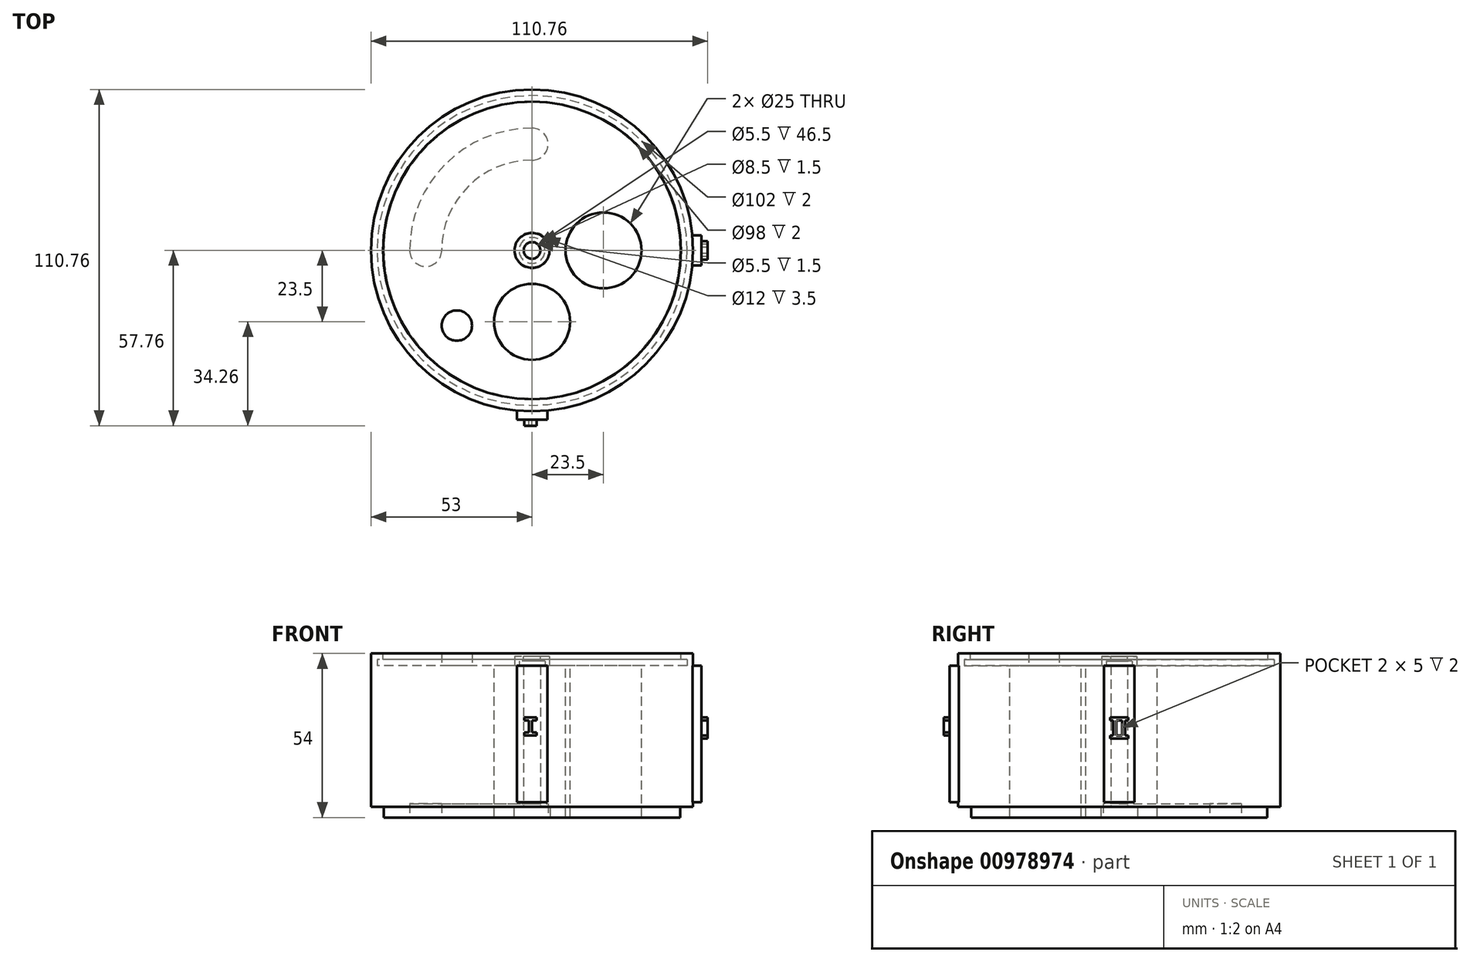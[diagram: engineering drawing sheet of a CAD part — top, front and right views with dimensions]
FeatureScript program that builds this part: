
annotation { "Feature Type Name" : "Feature", "Feature Type Description" : "" }
export const myFeature = defineFeature(function(context is Context, id is Id, definition is map)
    precondition{}
    {
        {
            var Q0;
            Q0=qCreatedBy(makeId("Top.planeOp"),FACE);
            var sketch = newSketch(context, id + "F0", { "sketchPlane" : qUnion([Q0])});
            skCircle(sketch, "E0", {"center": v(0, 0) * mm, "radius": 53 * mm});
            skCircle(sketch, "E1", {"center": v(0, 0) * mm, "radius": 2.75 * mm});
            skSolve(sketch);
        }
        {
            var Q0;
            Q0=makeQuery(id+"F0.imprint","IMPRINT",FACE,{"disambiguationData":[TD([[makeQuery(id+"F0.imprint","IMPRINT",EDGE,{"derivedFrom":sQuery(id+"F0.wireOp",EDGE,"E0")}),1.0]])]});
            extrude(context, id + "F1", {"entities" : qUnion([Q0]), "depth" : 50 * mm, "offsetDistance" : 25 * mm});
        }
        {
            var Q0;
            Q0=makeQuery(id+"F1.opExtrude","CAP_FACE",FACE,{"disambiguationData":[OSD([sQuery(id+"F0.wireOp",EDGE,"E0"),sQuery(id+"F0.wireOp",EDGE,"E1")])],"isStart":false});
            var sketch = newSketch(context, id + "F2", { "sketchPlane" : qUnion([Q0])});
            skCircle(sketch, "E2", {"center": v(0, 0) * mm, "radius": 51 * mm});
            skCircle(sketch, "E3", {"center": v(0, 0) * mm, "radius": 4.25 * mm});
            skCircle(sketch, "E4", {"center": v(0, 0) * mm, "radius": 5.75 * mm});
            skCircle(sketch, "E5", {"center": v(0, -23.5) * mm, "radius": 12.5 * mm});
            skCircle(sketch, "E6", {"center": v(23.5, 0) * mm, "radius": 12.5 * mm});
            skLineSegment(sketch, "E7", {"start": v(-5, -52.76) * mm, "end": v(-5, -55.76) * mm});
            skLineSegment(sketch, "E8", {"start": v(-5, -55.76) * mm, "end": v(5, -55.76) * mm});
            skLineSegment(sketch, "E9", {"start": v(5, -55.76) * mm, "end": v(5, -52.76) * mm});
            skLineSegment(sketch, "E10", {"start": v(52.76, 5) * mm, "end": v(55.76, 5) * mm});
            skLineSegment(sketch, "E11", {"start": v(55.76, 5) * mm, "end": v(55.76, -5) * mm});
            skLineSegment(sketch, "E12", {"start": v(55.76, -5) * mm, "end": v(52.76, -5) * mm});
            skLineSegment(sketch, "E13", {"start": v(0, 0) * mm, "end": v(-24.75, -24.75) * mm});
            skCircle(sketch, "E14", {"center": v(-24.75, -24.75) * mm, "radius": 5 * mm});
            skSolve(sketch);
        }
        {
            var Q0;
            Q0=makeQuery(id+"F2.imprint","IMPRINT",FACE,{"disambiguationData":[TD([[makeQuery(id+"F2.imprint","IMPRINT",EDGE,{"derivedFrom":sQuery(id+"F2.wireOp",EDGE,"E2")}),-1.0]])]});
            extrude(context, id + "F3", {"entities" : qUnion([Q0]), "operationType" : NewBodyOperationType.ADD, "depth" : 4 * mm, "offsetDistance" : 25 * mm});
        }
        {
            var Q0;
            Q0=makeQuery(id+"F3.opExtrude","CAP_FACE",FACE,{"disambiguationData":[OSD([sQuery(id+"F0.wireOp",EDGE,"E0"),sQuery(id+"F2.wireOp",EDGE,"E2")])],"isStart":false});
            var sketch = newSketch(context, id + "F4", { "sketchPlane" : qUnion([Q0])});
            skCircle(sketch, "E15", {"center": v(0, 0) * mm, "radius": 49 * mm});
            skSolve(sketch);
        }
        {
            var Q0;
            Q0=makeQuery(id+"F4.imprint","IMPRINT",FACE,{"disambiguationData":[TD([[makeQuery(id+"F4.imprint","IMPRINT",EDGE,{"derivedFrom":sQuery(id+"F4.wireOp",EDGE,"E15")}),-1.0]])]});
            extrude(context, id + "F5", {"entities" : qUnion([Q0]), "operationType" : NewBodyOperationType.ADD, "oppositeDirection" : true, "depth" : 2 * mm, "offsetDistance" : 25 * mm});
        }
        {
            var Q0;
            Q0=makeQuery(id+"F2.imprint","IMPRINT",FACE,{"disambiguationData":[TD([[makeQuery(id+"F2.imprint","IMPRINT",EDGE,{"derivedFrom":sQuery(id+"F2.wireOp",EDGE,"E3")}),-1.0]])]});
            extrude(context, id + "F6", {"entities" : qUnion([Q0]), "operationType" : NewBodyOperationType.ADD, "depth" : 3 * mm, "offsetDistance" : 25 * mm});
        }
        {
            var Q0;
            Q0=makeQuery(id+"F6.opExtrude","CAP_FACE",FACE,{"disambiguationData":[OSD([sQuery(id+"F2.wireOp",EDGE,"E3"),sQuery(id+"F2.wireOp",EDGE,"E4")])],"isStart":false});
            var sketch = newSketch(context, id + "F7", { "sketchPlane" : qUnion([Q0])});
            skCircle(sketch, "E16", {"center": v(0, 0) * mm, "radius": 2.75 * mm});
            skSolve(sketch);
        }
        {
            var Q0;
            Q0=makeQuery(id+"F7.imprint","IMPRINT",FACE,{"disambiguationData":[TD([[makeQuery(id+"F7.imprint","IMPRINT",EDGE,{"derivedFrom":sQuery(id+"F7.wireOp",EDGE,"E16")}),-1.0]])]});
            extrude(context, id + "F8", {"entities" : qUnion([Q0]), "operationType" : NewBodyOperationType.ADD, "oppositeDirection" : true, "depth" : 1.5 * mm, "offsetDistance" : 25 * mm});
        }
        {
            var Q0;
            Q0=makeQuery(id+"F1.opExtrude","CAP_FACE",FACE,{"disambiguationData":[OSD([sQuery(id+"F0.wireOp",EDGE,"E0"),sQuery(id+"F0.wireOp",EDGE,"E1")])],"isStart":true});
            var sketch = newSketch(context, id + "F9", { "sketchPlane" : qUnion([Q0])});
            skCircle(sketch, "E17", {"center": v(0, 0) * mm, "radius": 48.75 * mm});
            skCircle(sketch, "E18", {"center": v(0, 0) * mm, "radius": 6 * mm});
            skCircle(sketch, "E19", {"center": v(0, -35) * mm, "radius": 5.25 * mm});
            skCircle(sketch, "E20", {"center": v(-35, 0) * mm, "radius": 5.25 * mm});
            skCircle(sketch, "E21", {"center": v(0, 0) * mm, "radius": 29.75 * mm});
            skCircle(sketch, "E22", {"center": v(0, 0) * mm, "radius": 40.25 * mm});
            skSolve(sketch);
        }
        {
            var Q0;
            Q0=makeQuery(id+"F9.imprint","IMPRINT",FACE,{"disambiguationData":[TD([[makeQuery(id+"F9.imprint","IMPRINT",EDGE,{"derivedFrom":sQuery(id+"F9.wireOp",EDGE,"E17")}),-1.0]])]});
            var Q1;
            Q1=makeQuery(id+"F9.imprint","IMPRINT",FACE,{"disambiguationData":[TD([[makeQuery(id+"F9.imprint","IMPRINT",EDGE,{"derivedFrom":sQuery(id+"F9.wireOp",EDGE,"E18")}),1.0]])]});
            extrude(context, id + "F10", {"entities" : qUnion([Q0, Q1]), "operationType" : NewBodyOperationType.REMOVE, "oppositeDirection" : true, "depth" : 3.5 * mm, "offsetDistance" : 25 * mm});
        }
        {
            var Q0;
            {var subQ0=sQuery(id+"F9.wireOp",EDGE,"E20");var subQ1=makeQuery(id+"F9.imprint","INTERSECT",VERTEX,{"derivedFrom":[subQ0,sQuery(id+"F9.wireOp",EDGE,"E21")]});Q0=makeQuery(id+"F9.imprint","IMPRINT",FACE,{"disambiguationData":[TD([[makeQuery(id+"F9.imprint","IMPRINT",EDGE,{"disambiguationData":[TD([[subQ1,-1.0]])],"derivedFrom":subQ0}),1.0]])]});}
            var Q1;
            {var subQ0=sQuery(id+"F9.wireOp",EDGE,"E21");var subQ1=sQuery(id+"F9.wireOp",EDGE,"E19");var subQ2=makeQuery(id+"F9.imprint","INTERSECT",VERTEX,{"derivedFrom":[subQ1,subQ0]});Q1=makeQuery(id+"F9.imprint","IMPRINT",FACE,{"disambiguationData":[TD([[makeQuery(id+"F9.imprint","IMPRINT",EDGE,{"disambiguationData":[TD([[subQ2,-1.0]])],"derivedFrom":subQ1}),-1.0]])]});}
            var Q2;
            {var subQ0=sQuery(id+"F9.wireOp",EDGE,"E19");var subQ1=makeQuery(id+"F9.imprint","INTERSECT",VERTEX,{"derivedFrom":[subQ0,sQuery(id+"F9.wireOp",EDGE,"E21")]});Q2=makeQuery(id+"F9.imprint","IMPRINT",FACE,{"disambiguationData":[TD([[makeQuery(id+"F9.imprint","IMPRINT",EDGE,{"disambiguationData":[TD([[subQ1,-1.0]])],"derivedFrom":subQ0}),1.0]])]});}
            extrude(context, id + "F11", {"entities" : qUnion([Q0, Q1, Q2]), "operationType" : NewBodyOperationType.REMOVE, "oppositeDirection" : true, "depth" : 4.5 * mm, "offsetDistance" : 25 * mm});
        }
        {
            var Q0;
            Q0=makeQuery(id+"F2.imprint","IMPRINT",FACE,{"disambiguationData":[TD([[makeQuery(id+"F2.imprint","IMPRINT",EDGE,{"derivedFrom":sQuery(id+"F2.wireOp",EDGE,"E6")}),1.0]])]});
            extrude(context, id + "F12", {"entities" : qUnion([Q0]), "operationType" : NewBodyOperationType.REMOVE, "oppositeDirection" : true, "depth" : 100 * mm, "offsetDistance" : 25 * mm});
        }
        {
            var Q0;
            Q0=makeQuery(id+"F2.imprint","IMPRINT",FACE,{"disambiguationData":[TD([[makeQuery(id+"F2.imprint","IMPRINT",EDGE,{"derivedFrom":sQuery(id+"F2.wireOp",EDGE,"E5")}),1.0]])]});
            extrude(context, id + "F13", {"entities" : qUnion([Q0]), "operationType" : NewBodyOperationType.REMOVE, "oppositeDirection" : true, "depth" : 100 * mm, "offsetDistance" : 25 * mm});
        }
        {
            var Q0;
            {var subQ0=sQuery(id+"F2.wireOp",EDGE,"E7");Q0=makeQuery(id+"F2.imprint","IMPRINT",FACE,{"disambiguationData":[TD([[makeQuery(id+"F2.imprint","IMPRINT",EDGE,{"derivedFrom":subQ0}),1.0]])]});}
            var Q1;
            {var subQ0=sQuery(id+"F2.wireOp",EDGE,"E10");Q1=makeQuery(id+"F2.imprint","IMPRINT",FACE,{"disambiguationData":[TD([[makeQuery(id+"F2.imprint","IMPRINT",EDGE,{"derivedFrom":subQ0}),-1.0]])]});}
            extrude(context, id + "F14", {"entities" : qUnion([Q0, Q1]), "operationType" : NewBodyOperationType.ADD, "oppositeDirection" : true, "depth" : 45 * mm, "offsetDistance" : 25 * mm});
        }
        {
            var Q0;
            Q0=makeQuery(id+"F2.imprint","IMPRINT",FACE,{"disambiguationData":[TD([[makeQuery(id+"F2.imprint","IMPRINT",EDGE,{"derivedFrom":sQuery(id+"F2.wireOp",EDGE,"E14")}),1.0]])]});
            extrude(context, id + "F15", {"entities" : qUnion([Q0]), "operationType" : NewBodyOperationType.ADD, "depth" : 4 * mm, "offsetDistance" : 25 * mm});
        }
        {
            var Q0;
            Q0=makeQuery(id+"F14.opExtrude","SWEPT_FACE",FACE,{"disambiguationData":[OSD([sQuery(id+"F2.wireOp",EDGE,"E8")])]});
            var sketch = newSketch(context, id + "F16", { "sketchPlane" : qUnion([Q0])});
            skLineSegment(sketch, "E23", {"start": v(-2.5, 33) * mm, "end": v(1.5, 33) * mm});
            skLineSegment(sketch, "E24", {"start": v(1.5, 33) * mm, "end": v(1.5, 32) * mm});
            skLineSegment(sketch, "E25", {"start": v(1.5, 32) * mm, "end": v(0, 32) * mm});
            skLineSegment(sketch, "E26", {"start": v(0, 32) * mm, "end": v(0, 28) * mm});
            skLineSegment(sketch, "E27", {"start": v(0, 28) * mm, "end": v(1.5, 28) * mm});
            skLineSegment(sketch, "E28", {"start": v(1.5, 28) * mm, "end": v(1.5, 27) * mm});
            skLineSegment(sketch, "E29", {"start": v(1.5, 27) * mm, "end": v(-2.5, 27) * mm});
            skLineSegment(sketch, "E30", {"start": v(-2.5, 27) * mm, "end": v(-2.5, 28) * mm});
            skLineSegment(sketch, "E31", {"start": v(-2.5, 28) * mm, "end": v(-1, 28) * mm});
            skLineSegment(sketch, "E32", {"start": v(-1, 28) * mm, "end": v(-1, 32) * mm});
            skLineSegment(sketch, "E33", {"start": v(-1, 32) * mm, "end": v(-2.5, 32) * mm});
            skLineSegment(sketch, "E34", {"start": v(-2.5, 32) * mm, "end": v(-2.5, 33) * mm});
            skSolve(sketch);
        }
        {
            var Q0;
            Q0=makeQuery(id+"F16.imprint","IMPRINT",FACE,{"disambiguationData":[TD([[makeQuery(id+"F16.imprint","IMPRINT",EDGE,{"derivedFrom":sQuery(id+"F16.wireOp",EDGE,"E23")}),-1.0]])]});
            extrude(context, id + "F17", {"entities" : qUnion([Q0]), "operationType" : NewBodyOperationType.ADD, "depth" : 2 * mm, "offsetDistance" : 25 * mm});
        }
        {
            var Q0;
            Q0=makeQuery(id+"F14.opExtrude","SWEPT_FACE",FACE,{"disambiguationData":[OSD([sQuery(id+"F2.wireOp",EDGE,"E11")])]});
            var sketch = newSketch(context, id + "F18", { "sketchPlane" : qUnion([Q0])});
            skLineSegment(sketch, "E35", {"start": v(-3, 33) * mm, "end": v(3, 33) * mm});
            skLineSegment(sketch, "E36", {"start": v(3, 33) * mm, "end": v(3, 32) * mm});
            skLineSegment(sketch, "E37", {"start": v(3, 32) * mm, "end": v(2, 32) * mm});
            skLineSegment(sketch, "E38", {"start": v(2, 32) * mm, "end": v(2, 27) * mm});
            skLineSegment(sketch, "E39", {"start": v(2, 27) * mm, "end": v(3, 27) * mm});
            skLineSegment(sketch, "E40", {"start": v(3, 27) * mm, "end": v(3, 26) * mm});
            skLineSegment(sketch, "E41", {"start": v(3, 26) * mm, "end": v(-3, 26) * mm});
            skLineSegment(sketch, "E42", {"start": v(-3, 26) * mm, "end": v(-3, 27) * mm});
            skLineSegment(sketch, "E43", {"start": v(-3, 27) * mm, "end": v(-2, 27) * mm});
            skLineSegment(sketch, "E44", {"start": v(-2, 27) * mm, "end": v(-2, 32) * mm});
            skLineSegment(sketch, "E45", {"start": v(-2, 32) * mm, "end": v(-3, 32) * mm});
            skLineSegment(sketch, "E46", {"start": v(-3, 32) * mm, "end": v(-3, 33) * mm});
            skLineSegment(sketch, "E47", {"start": v(-1, 32) * mm, "end": v(1, 32) * mm});
            skLineSegment(sketch, "E48", {"start": v(1, 32) * mm, "end": v(1, 27) * mm});
            skLineSegment(sketch, "E49", {"start": v(1, 27) * mm, "end": v(-1, 27) * mm});
            skLineSegment(sketch, "E50", {"start": v(-1, 27) * mm, "end": v(-1, 32) * mm});
            skSolve(sketch);
        }
        {
            var Q0;
            Q0=makeQuery(id+"F18.imprint","IMPRINT",FACE,{"disambiguationData":[TD([[makeQuery(id+"F18.imprint","IMPRINT",EDGE,{"derivedFrom":sQuery(id+"F18.wireOp",EDGE,"E35")}),-1.0]])]});
            extrude(context, id + "F19", {"entities" : qUnion([Q0]), "operationType" : NewBodyOperationType.ADD, "depth" : 2 * mm, "offsetDistance" : 25 * mm});
        }
    });
